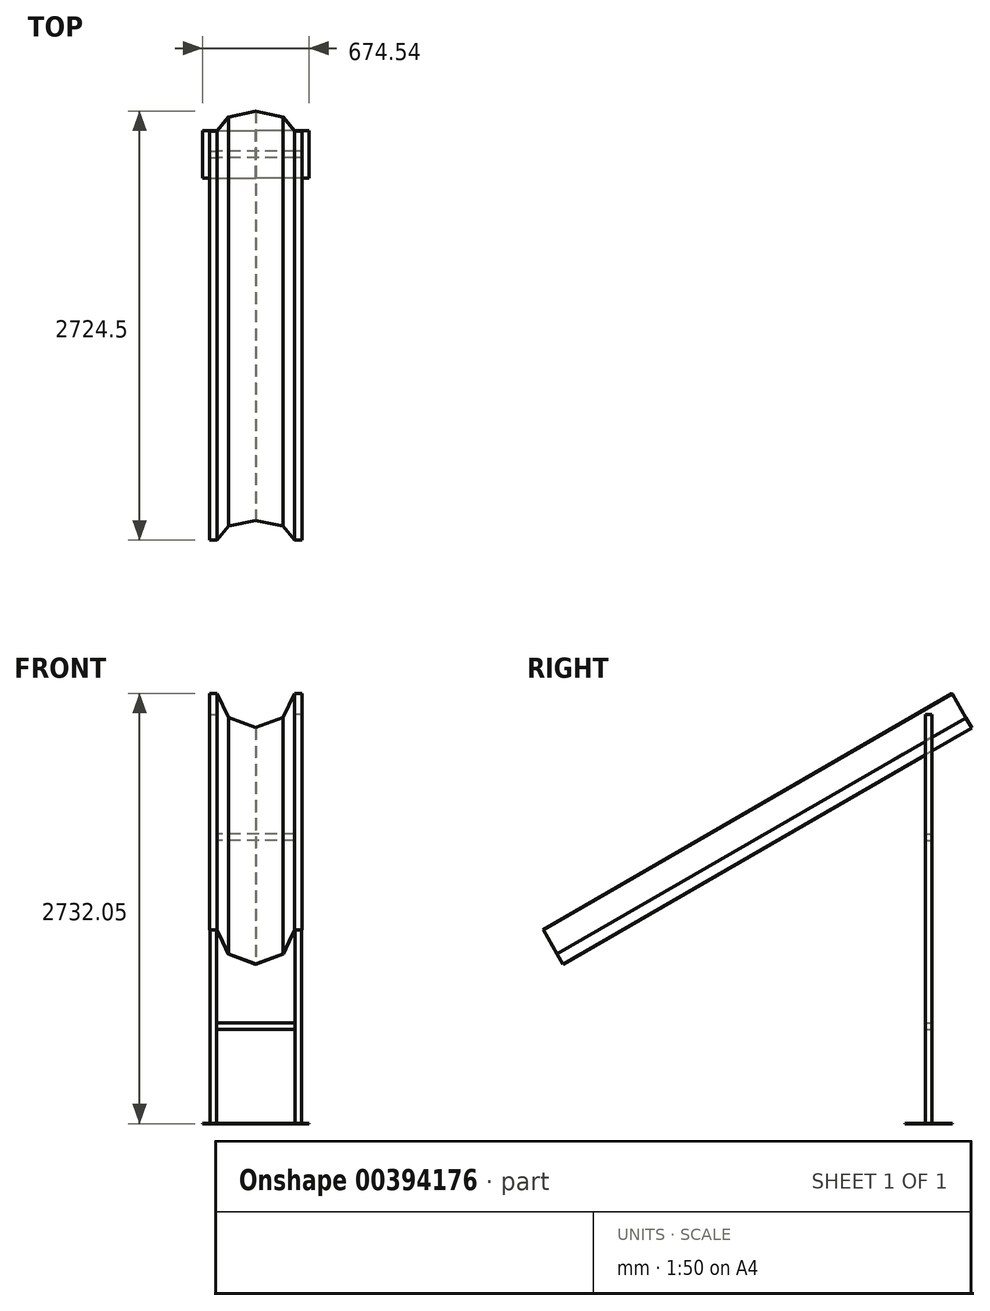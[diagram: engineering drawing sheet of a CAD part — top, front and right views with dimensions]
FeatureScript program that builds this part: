
annotation { "Feature Type Name" : "Feature", "Feature Type Description" : "" }
export const myFeature = defineFeature(function(context is Context, id is Id, definition is map)
    precondition{}
    {
        {
            var Q0;
            Q0=qCreatedBy(makeId("Front.planeOp"),FACE);
            var sketch = newSketch(context, id + "F0", { "sketchPlane" : qUnion([Q0])});
            skLineSegment(sketch, "E0.bottom", {"start": v(-59.56, 43.95) * mm, "end": v(-9.56, 43.95) * mm});
            skLineSegment(sketch, "E0.top", {"start": v(-59.56, 40.95) * mm, "end": v(-9.56, 40.95) * mm});
            skLineSegment(sketch, "E0.left", {"start": v(-59.56, 43.95) * mm, "end": v(-59.56, 40.95) * mm});
            skLineSegment(sketch, "E0.right", {"start": v(-9.56, 43.95) * mm, "end": v(-9.56, 40.95) * mm});
            skLineSegment(sketch, "E1.bottom", {"start": v(-9.56, 43.95) * mm, "end": v(61.99, -133.14) * mm});
            skLineSegment(sketch, "E1.top", {"start": v(-12.34, 42.83) * mm, "end": v(59.2, -134.26) * mm});
            skLineSegment(sketch, "E1.left", {"start": v(-9.56, 43.95) * mm, "end": v(-12.34, 42.83) * mm});
            skLineSegment(sketch, "E1.right", {"start": v(61.99, -133.14) * mm, "end": v(59.2, -134.26) * mm});
            skLineSegment(sketch, "E2.bottom", {"start": v(60.38, -131.5) * mm, "end": v(236.2, -206.13) * mm});
            skLineSegment(sketch, "E2.top", {"start": v(59.2, -134.26) * mm, "end": v(235.02, -208.9) * mm});
            skLineSegment(sketch, "E2.left", {"start": v(60.38, -131.5) * mm, "end": v(59.2, -134.26) * mm});
            skLineSegment(sketch, "E2.right", {"start": v(236.2, -206.13) * mm, "end": v(235.02, -208.9) * mm});
            skSolve(sketch);
        }
        {
            var Q0;
            Q0=makeQuery(id+"F0.imprint","IMPRINT",FACE,{"disambiguationData":[TD([[makeQuery(id+"F0.imprint","IMPRINT",EDGE,{"derivedFrom":sQuery(id+"F0.wireOp",EDGE,"E0.bottom")}),-1.0]])]});
            var Q1;
            {var subQ5=sQuery(id+"F0.wireOp",EDGE,"E0.right");Q1=makeQuery(id+"F0.imprint","IMPRINT",FACE,{"disambiguationData":[TD([[makeQuery(id+"F0.imprint","IMPRINT",EDGE,{"derivedFrom":subQ5}),1.0]])]});}
            var Q2;
            {var subQ4=sQuery(id+"F0.wireOp",EDGE,"E1.right");Q2=makeQuery(id+"F0.imprint","IMPRINT",FACE,{"disambiguationData":[TD([[makeQuery(id+"F0.imprint","IMPRINT",EDGE,{"derivedFrom":subQ4}),1.0]])]});}
            extrude(context, id + "F1", {"entities" : qUnion([Q0, Q1, Q2]), "oppositeDirection" : true, "depth" : 3000 * mm});
        }
        {
            var Q0;
            Q0=qCreatedBy(makeId("Top.planeOp"),FACE);
            var sketch = newSketch(context, id + "F2", { "sketchPlane" : qUnion([Q0])});
            skLineSegment(sketch, "E3.bottom", {"start": v(-54.56, 2800) * mm, "end": v(-14.56, 2800) * mm});
            skLineSegment(sketch, "E3.top", {"start": v(-54.56, 2760) * mm, "end": v(-14.56, 2760) * mm});
            skLineSegment(sketch, "E3.left", {"start": v(-54.56, 2800) * mm, "end": v(-54.56, 2760) * mm});
            skLineSegment(sketch, "E3.right", {"start": v(-14.56, 2800) * mm, "end": v(-14.56, 2760) * mm});
            skSolve(sketch);
        }
        {
            var Q0;
            Q0=makeQuery(id+"F2.imprint","IMPRINT",FACE,{"disambiguationData":[TD([[makeQuery(id+"F2.imprint","IMPRINT",EDGE,{"derivedFrom":sQuery(id+"F2.wireOp",EDGE,"E3.bottom")}),-1.0]])]});
            extrude(context, id + "F3", {"entities" : qUnion([Q0]), "oppositeDirection" : true, "depth" : 2600 * mm});
        }
        {
            var Q0;
            Q0=makeQuery(id+"F3.opExtrude","CAP_FACE",FACE,{"disambiguationData":[OSD([sQuery(id+"F2.wireOp",EDGE,"E3.bottom"),sQuery(id+"F2.wireOp",EDGE,"E3.top"),sQuery(id+"F2.wireOp",EDGE,"E3.left"),sQuery(id+"F2.wireOp",EDGE,"E3.right")])],"isStart":false});
            var sketch = newSketch(context, id + "F4", { "sketchPlane" : qUnion([Q0])});
            skLineSegment(sketch, "E4.bottom", {"start": v(-102.25, -2630) * mm, "end": v(236.2, -2630) * mm});
            skLineSegment(sketch, "E4.top", {"start": v(-102.25, -2930) * mm, "end": v(236.2, -2930) * mm});
            skLineSegment(sketch, "E4.left", {"start": v(-102.25, -2630) * mm, "end": v(-102.25, -2930) * mm});
            skLineSegment(sketch, "E4.right", {"start": v(236.2, -2630) * mm, "end": v(236.2, -2930) * mm});
            skSolve(sketch);
        }
        {
            var Q0;
            Q0=makeQuery(id+"F4.imprint","IMPRINT",FACE,{"disambiguationData":[TD([[makeQuery(id+"F4.imprint","IMPRINT",EDGE,{"derivedFrom":sQuery(id+"F4.wireOp",EDGE,"E4.bottom")}),-1.0]])]});
            var Q1;
            Q1=makeQuery(id+"F4.imprint","IMPRINT",FACE,{"disambiguationData":[TD([[makeQuery(id+"F4.imprint","IMPRINT",EDGE,{"derivedFrom":makeQuery(id+"F3.opExtrude","CAP_EDGE",EDGE,{"disambiguationData":[OSD([sQuery(id+"F2.wireOp",EDGE,"E3.bottom")])],"isStart":false})}),1.0]])]});
            extrude(context, id + "F5", {"entities" : qUnion([Q0, Q1]), "operationType" : NewBodyOperationType.ADD, "oppositeDirection" : true, "depth" : 3 * mm});
        }
        {
            var Q0;
            Q0=makeQuery(id+"F1.opExtrude","SWEPT_EDGE",EDGE,{"disambiguationData":[OSD([sQuery(id+"F0.wireOp",EDGE,"E2.top"),sQuery(id+"F0.wireOp",EDGE,"E2.right")])]});
            cPlane(context, id + "F6", {"entities" : qUnion([Q0]), "cplaneType" : CPlaneType.LINE_ANGLE, "offset" : 25 * mm, "angle" : 90 * degree, "width" : 150 * mm, "height" : 150 * mm});
        }
        {
            var Q0;
            Q0=makeQuery(id+"F3.opExtrude","SWEPT_BODY",BODY,{"disambiguationData":[OSD([sQuery(id+"F2.wireOp",EDGE,"E3.bottom"),sQuery(id+"F2.wireOp",EDGE,"E3.top"),sQuery(id+"F2.wireOp",EDGE,"E3.left"),sQuery(id+"F2.wireOp",EDGE,"E3.right")])]});
            var Q1;
            Q1=makeQuery(id+"F1.opExtrude","SWEPT_BODY",BODY,{"disambiguationData":[OSD([sQuery(id+"F0.wireOp",EDGE,"E0.bottom"),sQuery(id+"F0.wireOp",EDGE,"E0.top"),sQuery(id+"F0.wireOp",EDGE,"E0.left"),sQuery(id+"F0.wireOp",EDGE,"E1.top"),sQuery(id+"F0.wireOp",EDGE,"E1.left")])]});
            var Q2;
            Q2=makeQuery(id+"F1.opExtrude","SWEPT_BODY",BODY,{"disambiguationData":[OSD([sQuery(id+"F0.wireOp",EDGE,"E0.top"),sQuery(id+"F0.wireOp",EDGE,"E0.right"),sQuery(id+"F0.wireOp",EDGE,"E1.bottom"),sQuery(id+"F0.wireOp",EDGE,"E1.top"),sQuery(id+"F0.wireOp",EDGE,"E2.bottom"),sQuery(id+"F0.wireOp",EDGE,"E2.left")])]});
            var Q3;
            Q3=makeQuery(id+"F1.opExtrude","SWEPT_BODY",BODY,{"disambiguationData":[OSD([sQuery(id+"F0.wireOp",EDGE,"E1.bottom"),sQuery(id+"F0.wireOp",EDGE,"E1.right"),sQuery(id+"F0.wireOp",EDGE,"E2.bottom"),sQuery(id+"F0.wireOp",EDGE,"E2.top"),sQuery(id+"F0.wireOp",EDGE,"E2.right")])]});
            var Q4;
            Q4=qCreatedBy(id+"F6.planeOp",FACE);
            mirror(context, id + "F7", {"entities" : qUnion([Q0, Q1, Q2, Q3]), "mirrorPlane" : qUnion([Q4])});
        }
        {
            var Q0;
            Q0=makeQuery(id+"F3.opExtrude","SWEPT_FACE",FACE,{"disambiguationData":[OSD([sQuery(id+"F2.wireOp",EDGE,"E3.right")])]});
            var sketch = newSketch(context, id + "F8", { "sketchPlane" : qUnion([Q0])});
            skLineSegment(sketch, "E5.bottom", {"start": v(2760, -760) * mm, "end": v(2800, -760) * mm});
            skLineSegment(sketch, "E5.top", {"start": v(2760, -800) * mm, "end": v(2800, -800) * mm});
            skLineSegment(sketch, "E5.left", {"start": v(2760, -760) * mm, "end": v(2760, -800) * mm});
            skLineSegment(sketch, "E5.right", {"start": v(2800, -760) * mm, "end": v(2800, -800) * mm});
            skLineSegment(sketch, "E6.bottom", {"start": v(2760, -1960) * mm, "end": v(2800, -1960) * mm});
            skLineSegment(sketch, "E6.top", {"start": v(2760, -2000) * mm, "end": v(2800, -2000) * mm});
            skLineSegment(sketch, "E6.left", {"start": v(2760, -1960) * mm, "end": v(2760, -2000) * mm});
            skLineSegment(sketch, "E6.right", {"start": v(2800, -1960) * mm, "end": v(2800, -2000) * mm});
            skSolve(sketch);
        }
        {
            var Q0;
            Q0=makeQuery(id+"F8.imprint","IMPRINT",FACE,{"disambiguationData":[TD([[makeQuery(id+"F8.imprint","IMPRINT",EDGE,{"derivedFrom":sQuery(id+"F8.wireOp",EDGE,"E5.bottom")}),-1.0]])]});
            var Q1;
            Q1=makeQuery(id+"F8.imprint","IMPRINT",FACE,{"disambiguationData":[TD([[makeQuery(id+"F8.imprint","IMPRINT",EDGE,{"derivedFrom":sQuery(id+"F8.wireOp",EDGE,"E6.bottom")}),-1.0]])]});
            extrude(context, id + "F9", {"entities" : qUnion([Q0, Q1]), "endBound" : BoundingType.UP_TO_NEXT, "depth" : 25 * mm});
        }
        {
            var Q0;
            Q0=makeQuery(id+"F7.opPattern","COPY",FACE,{"derivedFrom":makeQuery(id+"F3.opExtrude","SWEPT_FACE",FACE,{"disambiguationData":[OSD([sQuery(id+"F2.wireOp",EDGE,"E3.bottom")])]}),"instanceName":"1"});
            var sketch = newSketch(context, id + "F10", { "sketchPlane" : qUnion([Q0])});
            skLineSegment(sketch, "E7", {"start": v(-614.11, -44.92) * mm, "end": v(227.85, -44.92) * mm, "construction": true});
            skSolve(sketch);
        }
        {
            var Q0;
            Q0=makeQuery(id+"F7.opPattern","COPY",BODY,{"derivedFrom":makeQuery(id+"F1.opExtrude","SWEPT_BODY",BODY,{"disambiguationData":[OSD([sQuery(id+"F0.wireOp",EDGE,"E0.top"),sQuery(id+"F0.wireOp",EDGE,"E0.right"),sQuery(id+"F0.wireOp",EDGE,"E1.bottom"),sQuery(id+"F0.wireOp",EDGE,"E1.top"),sQuery(id+"F0.wireOp",EDGE,"E2.bottom"),sQuery(id+"F0.wireOp",EDGE,"E2.left")])]}),"instanceName":"1"});
            var Q1;
            Q1=makeQuery(id+"F7.opPattern","COPY",BODY,{"derivedFrom":makeQuery(id+"F1.opExtrude","SWEPT_BODY",BODY,{"disambiguationData":[OSD([sQuery(id+"F0.wireOp",EDGE,"E1.bottom"),sQuery(id+"F0.wireOp",EDGE,"E1.right"),sQuery(id+"F0.wireOp",EDGE,"E2.bottom"),sQuery(id+"F0.wireOp",EDGE,"E2.top"),sQuery(id+"F0.wireOp",EDGE,"E2.right")])]}),"instanceName":"1"});
            var Q2;
            Q2=makeQuery(id+"F7.opPattern","COPY",BODY,{"derivedFrom":makeQuery(id+"F1.opExtrude","SWEPT_BODY",BODY,{"disambiguationData":[OSD([sQuery(id+"F0.wireOp",EDGE,"E0.bottom"),sQuery(id+"F0.wireOp",EDGE,"E0.top"),sQuery(id+"F0.wireOp",EDGE,"E0.left"),sQuery(id+"F0.wireOp",EDGE,"E1.top"),sQuery(id+"F0.wireOp",EDGE,"E1.left")])]}),"instanceName":"1"});
            var Q3;
            Q3=makeQuery(id+"F1.opExtrude","SWEPT_BODY",BODY,{"disambiguationData":[OSD([sQuery(id+"F0.wireOp",EDGE,"E1.bottom"),sQuery(id+"F0.wireOp",EDGE,"E1.right"),sQuery(id+"F0.wireOp",EDGE,"E2.bottom"),sQuery(id+"F0.wireOp",EDGE,"E2.top"),sQuery(id+"F0.wireOp",EDGE,"E2.right")])]});
            var Q4;
            Q4=makeQuery(id+"F1.opExtrude","SWEPT_BODY",BODY,{"disambiguationData":[OSD([sQuery(id+"F0.wireOp",EDGE,"E0.top"),sQuery(id+"F0.wireOp",EDGE,"E0.right"),sQuery(id+"F0.wireOp",EDGE,"E1.bottom"),sQuery(id+"F0.wireOp",EDGE,"E1.top"),sQuery(id+"F0.wireOp",EDGE,"E2.bottom"),sQuery(id+"F0.wireOp",EDGE,"E2.left")])]});
            var Q5;
            Q5=makeQuery(id+"F1.opExtrude","SWEPT_BODY",BODY,{"disambiguationData":[OSD([sQuery(id+"F0.wireOp",EDGE,"E0.bottom"),sQuery(id+"F0.wireOp",EDGE,"E0.top"),sQuery(id+"F0.wireOp",EDGE,"E0.left"),sQuery(id+"F0.wireOp",EDGE,"E1.top"),sQuery(id+"F0.wireOp",EDGE,"E1.left")])]});
            var Q6;
            Q6=sQuery(id+"F10.wireOp",EDGE,"E7");
            transform(context, id + "F11", {"entities" : qUnion([Q0, Q1, Q2, Q3, Q4, Q5]), "transformType" : TransformType.ROTATION, "transformAxis" : qUnion([Q6]), "angle" : 30 * degree, "oppositeDirection" : true, "makeCopy" : false});
        }
    });
